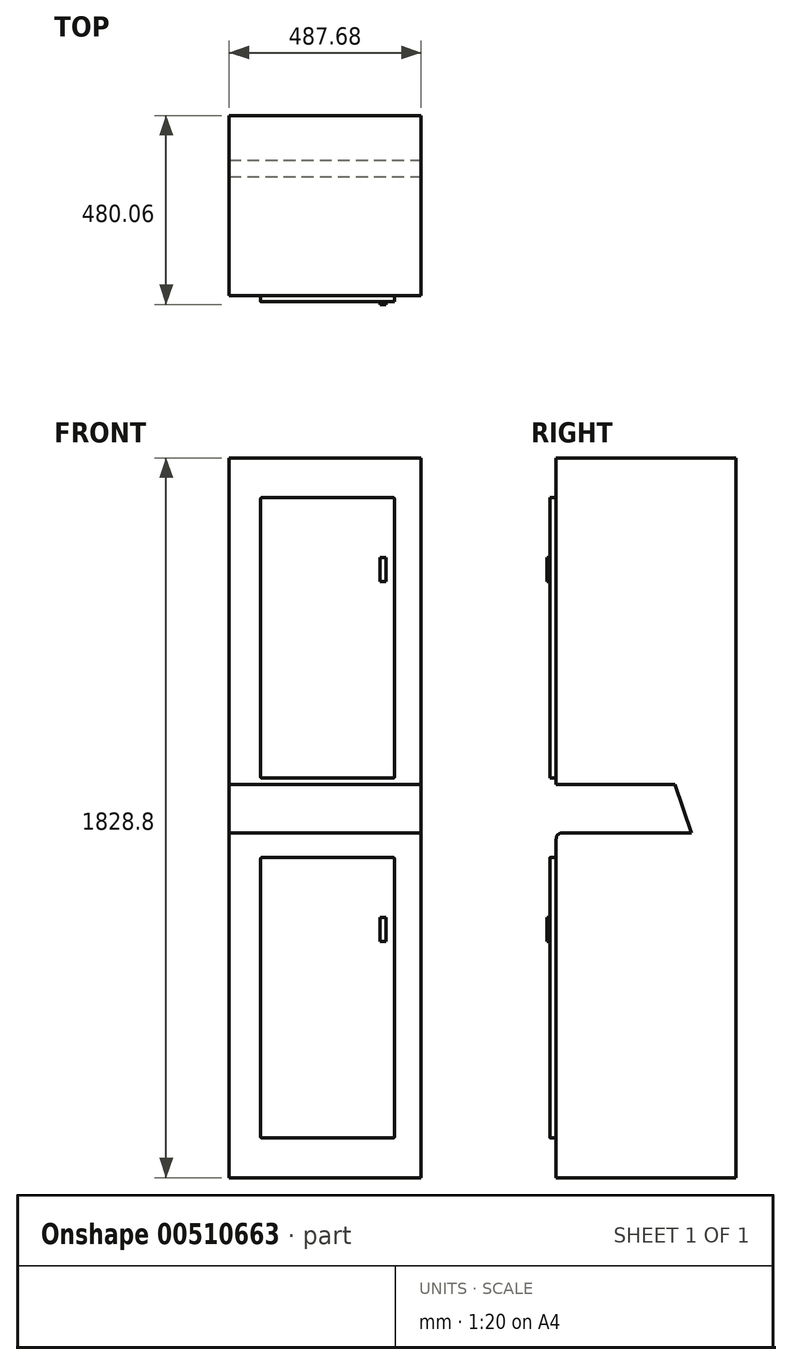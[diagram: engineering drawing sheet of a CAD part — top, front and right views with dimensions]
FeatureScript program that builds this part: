
annotation { "Feature Type Name" : "Feature", "Feature Type Description" : "" }
export const myFeature = defineFeature(function(context is Context, id is Id, definition is map)
    precondition{}
    {
        {
            var Q0;
            Q0=qCreatedBy(makeId("Top.planeOp"),FACE);
            var sketch = newSketch(context, id + "F0", { "sketchPlane" : qUnion([Q0])});
            skLineSegment(sketch, "E0.bottom", {"start": v(-260.53, 228.7) * mm, "end": v(227.15, 228.7) * mm});
            skLineSegment(sketch, "E0.top", {"start": v(-260.53, -228.5) * mm, "end": v(227.15, -228.5) * mm});
            skLineSegment(sketch, "E0.left", {"start": v(-260.53, 228.7) * mm, "end": v(-260.53, -228.5) * mm});
            skLineSegment(sketch, "E0.right", {"start": v(227.15, 228.7) * mm, "end": v(227.15, -228.5) * mm});
            skSolve(sketch);
        }
        {
            var Q0;
            Q0 = qSketchRegion(id + "F0", true);
            extrude(context, id + "F1", {"entities" : qUnion([Q0]), "depth" : 914.4 * mm, "offsetDistance" : 30.48 * mm});
        }
        {
            var Q0;
            Q0=makeQuery(id+"F1.opExtrude","SWEPT_FACE",FACE,{"disambiguationData":[OSD([sQuery(id+"F0.wireOp",EDGE,"E0.top")])]});
            var sketch = newSketch(context, id + "F2", { "sketchPlane" : qUnion([Q0])});
            skLineSegment(sketch, "E1.bottom", {"start": v(-176.46, 100.58) * mm, "end": v(154.59, 100.58) * mm});
            skLineSegment(sketch, "E1.top", {"start": v(-176.46, 813.82) * mm, "end": v(154.59, 813.82) * mm});
            skLineSegment(sketch, "E1.left", {"start": v(-181.46, 105.58) * mm, "end": v(-181.46, 808.82) * mm});
            skLineSegment(sketch, "E1.right", {"start": v(159.59, 105.58) * mm, "end": v(159.59, 808.82) * mm});
            skPoint(sketch, "E2.visualSharp", {"position": v(-181.46, 813.82) * mm});
            skArc(sketch, "E2.filletArc", {"start": v(-176.46, 813.82) * mm, "mid": v(-180, 812.35) * mm, "end": v(-181.46, 808.82) * mm});
            skPoint(sketch, "E3.visualSharp", {"position": v(159.59, 813.82) * mm});
            skArc(sketch, "E3.filletArc", {"start": v(159.59, 808.82) * mm, "mid": v(158.12, 812.35) * mm, "end": v(154.59, 813.82) * mm});
            skPoint(sketch, "E4.visualSharp", {"position": v(159.59, 100.58) * mm});
            skArc(sketch, "E4.filletArc", {"start": v(154.59, 100.58) * mm, "mid": v(158.12, 102.05) * mm, "end": v(159.59, 105.58) * mm});
            skPoint(sketch, "E5.visualSharp", {"position": v(-181.46, 100.58) * mm});
            skArc(sketch, "E5.filletArc", {"start": v(-181.46, 105.58) * mm, "mid": v(-180, 102.05) * mm, "end": v(-176.46, 100.58) * mm});
            skSolve(sketch);
        }
        {
            var Q0;
            Q0 = qSketchRegion(id + "F2", true);
            extrude(context, id + "F3", {"entities" : qUnion([Q0]), "operationType" : NewBodyOperationType.ADD, "depth" : 15.24 * mm, "offsetDistance" : 30.48 * mm});
        }
        {
            var Q0;
            Q0=makeQuery(id+"F1.opExtrude","SWEPT_BODY",BODY,{"disambiguationData":[OSD([sQuery(id+"F0.wireOp",EDGE,"E0.bottom"),sQuery(id+"F0.wireOp",EDGE,"E0.top"),sQuery(id+"F0.wireOp",EDGE,"E0.left"),sQuery(id+"F0.wireOp",EDGE,"E0.right")])]});
            var Q1;
            Q1=makeQuery(id+"F1.opExtrude","CAP_FACE",FACE,{"disambiguationData":[OSD([sQuery(id+"F0.wireOp",EDGE,"E0.bottom"),sQuery(id+"F0.wireOp",EDGE,"E0.top"),sQuery(id+"F0.wireOp",EDGE,"E0.left"),sQuery(id+"F0.wireOp",EDGE,"E0.right")])],"isStart":true});
            mirror(context, id + "F4", {"operationType" : NewBodyOperationType.ADD, "entities" : qUnion([Q0]), "mirrorPlane" : qUnion([Q1])});
        }
        {
            var Q0;
            Q0=makeQuery(id+"F3.opExtrude","CAP_FACE",FACE,{"disambiguationData":[OSD([sQuery(id+"F2.wireOp",EDGE,"E1.bottom"),sQuery(id+"F2.wireOp",EDGE,"E1.top"),sQuery(id+"F2.wireOp",EDGE,"E1.left"),sQuery(id+"F2.wireOp",EDGE,"E1.right"),sQuery(id+"F2.wireOp",EDGE,"E2.filletArc"),sQuery(id+"F2.wireOp",EDGE,"E3.filletArc"),sQuery(id+"F2.wireOp",EDGE,"E4.filletArc"),sQuery(id+"F2.wireOp",EDGE,"E5.filletArc")])],"isStart":false});
            var sketch = newSketch(context, id + "F5", { "sketchPlane" : qUnion([Q0])});
            skLineSegment(sketch, "E6", {"start": v(123.01, 661.42) * mm, "end": v(138.25, 661.42) * mm});
            skLineSegment(sketch, "E7", {"start": v(138.25, 661.42) * mm, "end": v(138.25, 600.46) * mm});
            skLineSegment(sketch, "E8", {"start": v(138.25, 600.46) * mm, "end": v(123.01, 600.46) * mm});
            skLineSegment(sketch, "E9", {"start": v(123.01, 600.46) * mm, "end": v(123.01, 661.42) * mm});
            skLineSegment(sketch, "E10", {"start": v(123.01, -252.98) * mm, "end": v(138.25, -252.98) * mm});
            skLineSegment(sketch, "E11", {"start": v(138.25, -252.98) * mm, "end": v(138.25, -313.94) * mm});
            skLineSegment(sketch, "E12", {"start": v(138.25, -313.94) * mm, "end": v(123.01, -313.94) * mm});
            skLineSegment(sketch, "E13", {"start": v(123.01, -313.94) * mm, "end": v(123.01, -252.98) * mm});
            skSolve(sketch);
        }
        {
            var Q0;
            Q0 = qSketchRegion(id + "F5", true);
            extrude(context, id + "F6", {"entities" : qUnion([Q0]), "operationType" : NewBodyOperationType.ADD, "depth" : 7.62 * mm, "offsetDistance" : 30.48 * mm});
        }
        {
            var Q0;
            {var subQ0=makeQuery(id+"F1.opExtrude","SWEPT_FACE",FACE,{"disambiguationData":[OSD([sQuery(id+"F0.wireOp",EDGE,"E0.right")])]});Q0=makeQuery(id+"F4.boolean.opBoolean","MERGE",FACE,{"derivedFrom":[subQ0,makeQuery(id+"F4.opPattern","COPY",FACE,{"derivedFrom":subQ0,"instanceName":"1"})]});}
            var sketch = newSketch(context, id + "F7", { "sketchPlane" : qUnion([Q0])});
            skLineSegment(sketch, "E14", {"start": v(-228.5, 84.02) * mm, "end": v(72.72, 84.02) * mm});
            skLineSegment(sketch, "E15", {"start": v(72.72, 84.02) * mm, "end": v(115.45, -38.5) * mm});
            skLineSegment(sketch, "E16", {"start": v(115.45, -38.5) * mm, "end": v(-228.5, -38.5) * mm});
            skLineSegment(sketch, "E17", {"start": v(-228.5, -38.5) * mm, "end": v(-228.5, 84.02) * mm});
            skSolve(sketch);
        }
        {
            var Q0;
            Q0 = qSketchRegion(id + "F7", true);
            extrude(context, id + "F8", {"entities" : qUnion([Q0]), "operationType" : NewBodyOperationType.REMOVE, "oppositeDirection" : true, "depth" : 487.68 * mm, "offsetDistance" : 30.48 * mm});
        }
        {
            var Q0;
            Q0=makeQuery(id+"F8.boolean.opBoolean","COPY",EDGE,{"derivedFrom":makeQuery(id+"F8.opExtrude","SWEPT_EDGE",EDGE,{"disambiguationData":[OSD([sQuery(id+"F0.wireOp",EDGE,"E0.top"),sQuery(id+"F0.wireOp",EDGE,"E0.right"),sQuery(id+"F7.wireOp",EDGE,"E16"),sQuery(id+"F7.wireOp",EDGE,"E17")])]})});
            var Q1;
            Q1=makeQuery(id+"F8.boolean.opBoolean","COPY",EDGE,{"derivedFrom":makeQuery(id+"F8.opExtrude","SWEPT_EDGE",EDGE,{"disambiguationData":[OSD([sQuery(id+"F0.wireOp",EDGE,"E0.top"),sQuery(id+"F0.wireOp",EDGE,"E0.right"),sQuery(id+"F7.wireOp",EDGE,"E14"),sQuery(id+"F7.wireOp",EDGE,"E17")])]})});
            fillet(context, id + "F9", {"entities" : qUnion([Q0, Q1]), "radius" : 15.24 * mm, "tangentPropagation" : true, "allowEdgeOverflow" : false});
        }
    });
